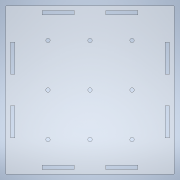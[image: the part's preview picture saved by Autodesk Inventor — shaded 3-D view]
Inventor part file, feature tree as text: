
AUTODESK INVENTOR PART (.ipt)
format: ipt  version: 2021 (Build 250183000, 183)  size: 202,752 bytes
history: native  units: mm
features: sketch x11, hole x9, extrude x2
ambient origin geometry x8: Origin, YZ Plane, XZ Plane, XY Plane, X Axis, Y Axis, Z Axis, Center Point
bodies: Solid1 (feature_tree)
feature tree (22):
  extrude  "Extrusion1"  Depth=106.0mm
  hole  "Hole1"  [1 undecoded]
  sketch  "Sketch3"  dims[d7=1.0mm d8=1.0mm]
  hole  "Hole2"  [1 undecoded]
  hole  "Hole3"  [1 undecoded]
  hole  "Hole4"  [1 undecoded]
  hole  "Hole5"  [1 undecoded]
  hole  "Hole6"  [1 undecoded]
  hole  "Hole7"  [1 undecoded]
  hole  "Hole8"  [1 undecoded]
  hole  "Hole9"  [1 undecoded]
  extrude  "Extrusion2"  Depth=3.0mm
  sketch  "Sketch1"  dims[d0=106.0mm d1=106.0mm]
  sketch  "Sketch2"  dims[d4=3.0mm d5=0.0mm d6=1.0mm]
  sketch  "Sketch5"  dims[d9=1.0mm d10=1.0mm]
  sketch  "Sketch6"  dims[d11=1.0mm d12=1.0mm]
  sketch  "Sketch7"  dims[d13=1.0mm d14=1.0mm]
  sketch  "Sketch8"  dims[d15=3.0mm d16=6.0mm d17=4.0mm d18=2.0mm d19=90.0deg d20=8.0mm d21=20.594885mm d22=3.0mm]
  sketch  "Sketch9"  dims[d23=3.0mm d24=3.0mm]
  sketch  "Sketch10"  dims[d25=3.0mm d26=3.0mm]
  sketch  "Sketch11"  dims[d27=3.0mm d28=3.0mm]
  sketch  "Sketch12"  dims[d29=3.0mm d30=3.0mm d31=6.0mm d32=4.0mm d33=2.0mm d34=90.0deg d35=8.0mm d36=20.594885mm d37=3.0mm d38=3.0mm d39=6.0mm d40=4.0mm d41=2.0mm d42=90.0deg d43=8.0mm d44=20.594885mm d45=3.0mm d46=3.0mm d47=6.0mm d48=4.0mm d49=2.0mm d50=90.0deg d51=8.0mm d52=20.594885mm d53=3.0mm d54=3.0mm d55=6.0mm d56=4.0mm d57=2.0mm d58=90.0deg d59=8.0mm d60=20.594885mm d61=3.0mm d62=3.0mm d63=6.0mm d64=4.0mm d65=2.0mm d66=90.0deg d67=8.0mm d68=20.594885mm d69=3.0mm d70=3.0mm d71=6.0mm d72=4.0mm d73=2.0mm d74=90.0deg d75=8.0mm d76=20.594885mm d77=3.0mm d78=3.0mm d79=6.0mm d80=4.0mm d81=2.0mm d82=90.0deg d83=8.0mm d84=20.594885mm d85=3.0mm d86=3.0mm d87=6.0mm d88=4.0mm d89=2.0mm d90=90.0deg d91=8.0mm d92=20.594885mm d99=112.0mm d100=112.0mm d101=3.0mm d102=0.0mm d103=0.5mm d104=0.872665mm]
note: 9 required parameter values undecoded (feature->parameter linkage not recoverable at this tier; creation-order binding heuristic only, values carry confidence <= 0.55)
